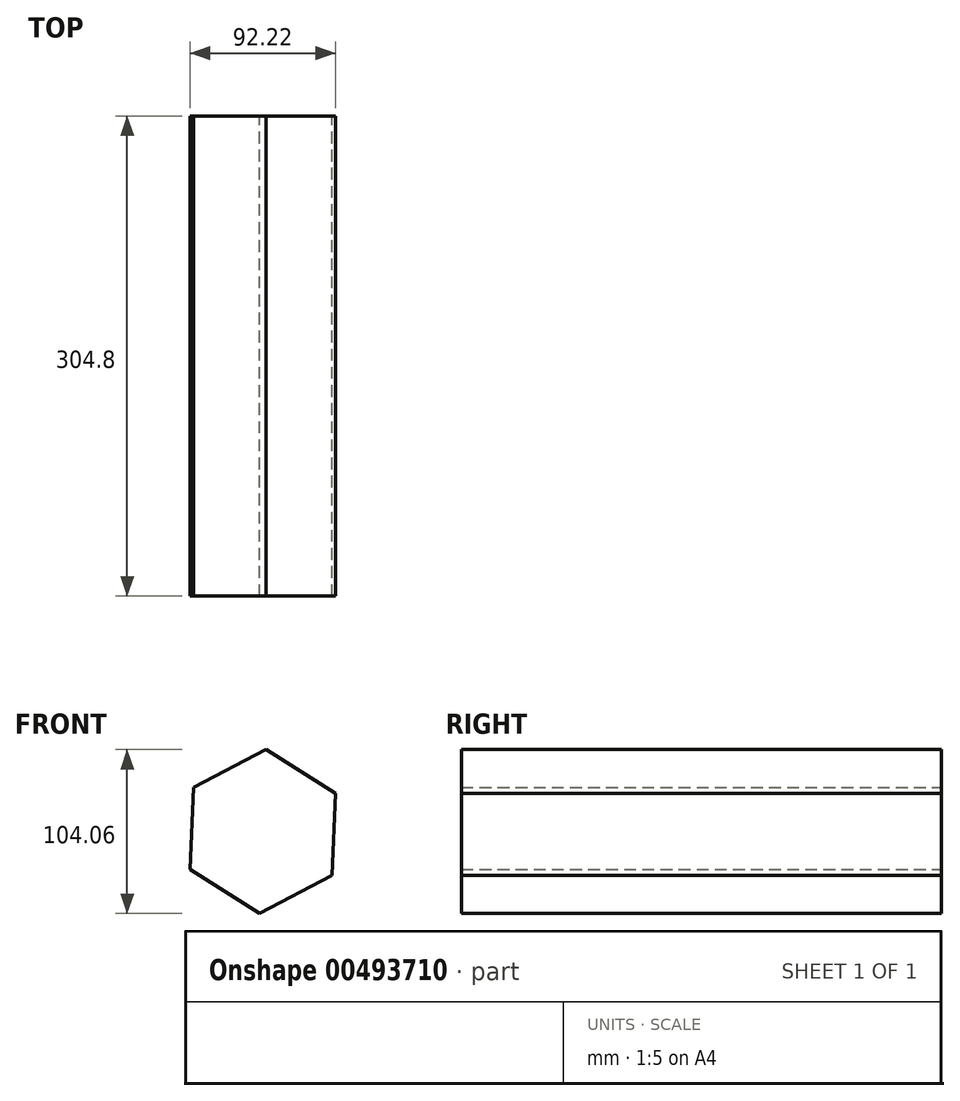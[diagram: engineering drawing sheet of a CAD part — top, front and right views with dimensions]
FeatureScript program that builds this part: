
annotation { "Feature Type Name" : "Feature", "Feature Type Description" : "" }
export const myFeature = defineFeature(function(context is Context, id is Id, definition is map)
    precondition{}
    {
        {
            var Q0;
            Q0=qCreatedBy(makeId("Front.planeOp"),FACE);
            var sketch = newSketch(context, id + "F0", { "sketchPlane" : qUnion([Q0])});
            skCircle(sketch, "E0.cCircle", {"center": v(0, 0) * mm, "radius": 52.08 * mm, "construction": true});
            skLineSegment(sketch, "E0.0", {"start": v(-44.01, 27.84) * mm, "end": v(2.1, 52.03) * mm});
            skLineSegment(sketch, "E0.1", {"start": v(2.1, 52.03) * mm, "end": v(46.11, 24.2) * mm});
            skLineSegment(sketch, "E0.2", {"start": v(46.11, 24.2) * mm, "end": v(44.01, -27.84) * mm});
            skLineSegment(sketch, "E0.3", {"start": v(44.01, -27.84) * mm, "end": v(-2.1, -52.03) * mm});
            skLineSegment(sketch, "E0.4", {"start": v(-2.1, -52.03) * mm, "end": v(-46.11, -24.2) * mm});
            skLineSegment(sketch, "E0.5", {"start": v(-46.11, -24.2) * mm, "end": v(-44.01, 27.84) * mm});
            skSolve(sketch);
        }
        {
            var Q0;
            Q0=makeQuery(id+"F0.imprint","IMPRINT",FACE,{"disambiguationData":[TD([[makeQuery(id+"F0.imprint","IMPRINT",EDGE,{"derivedFrom":sQuery(id+"F0.wireOp",EDGE,"E0.0")}),-1.0]])]});
            extrude(context, id + "F1", {"entities" : qUnion([Q0]), "depth" : 304.8 * mm});
        }
    });
